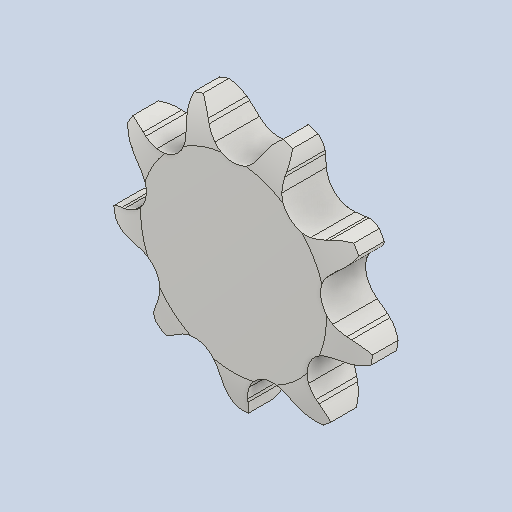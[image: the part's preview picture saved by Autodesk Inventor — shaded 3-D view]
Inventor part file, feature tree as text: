
AUTODESK INVENTOR PART (.ipt)
format: ipt  version: 2022.1 (Build 261234000, 234)  size: 371,200 bytes
history: native  units: mm
features: other x6, extrude x2, pattern_linear x1, pattern_circular x1
ambient origin geometry x8: Origin, YZ Plane, XZ Plane, XY Plane, X Axis, Y Axis, Z Axis, Center Point
bodies: Solid1 (feature_tree)
feature tree (10):
  other  "Perfil de diente teórico"
  other  "Perfil de diente"
  other  "Perfil de sección"
  other  "Cubierta"
  other  "Ramal"
  pattern_linear  "Patrón de ramal"  Spacing1=46.415395mm  [1 undecoded]
  extrude  "Diente teórico"  Depth=6.981317mm
  extrude  "Diente"  Depth=5.1308mm
  pattern_circular  "Patrón de diente"  [2 undecoded]
  other  "Plano síncrono"
note: 3 required parameter values undecoded (feature->parameter linkage not recoverable at this tier; creation-order binding heuristic only, values carry confidence <= 0.55)
